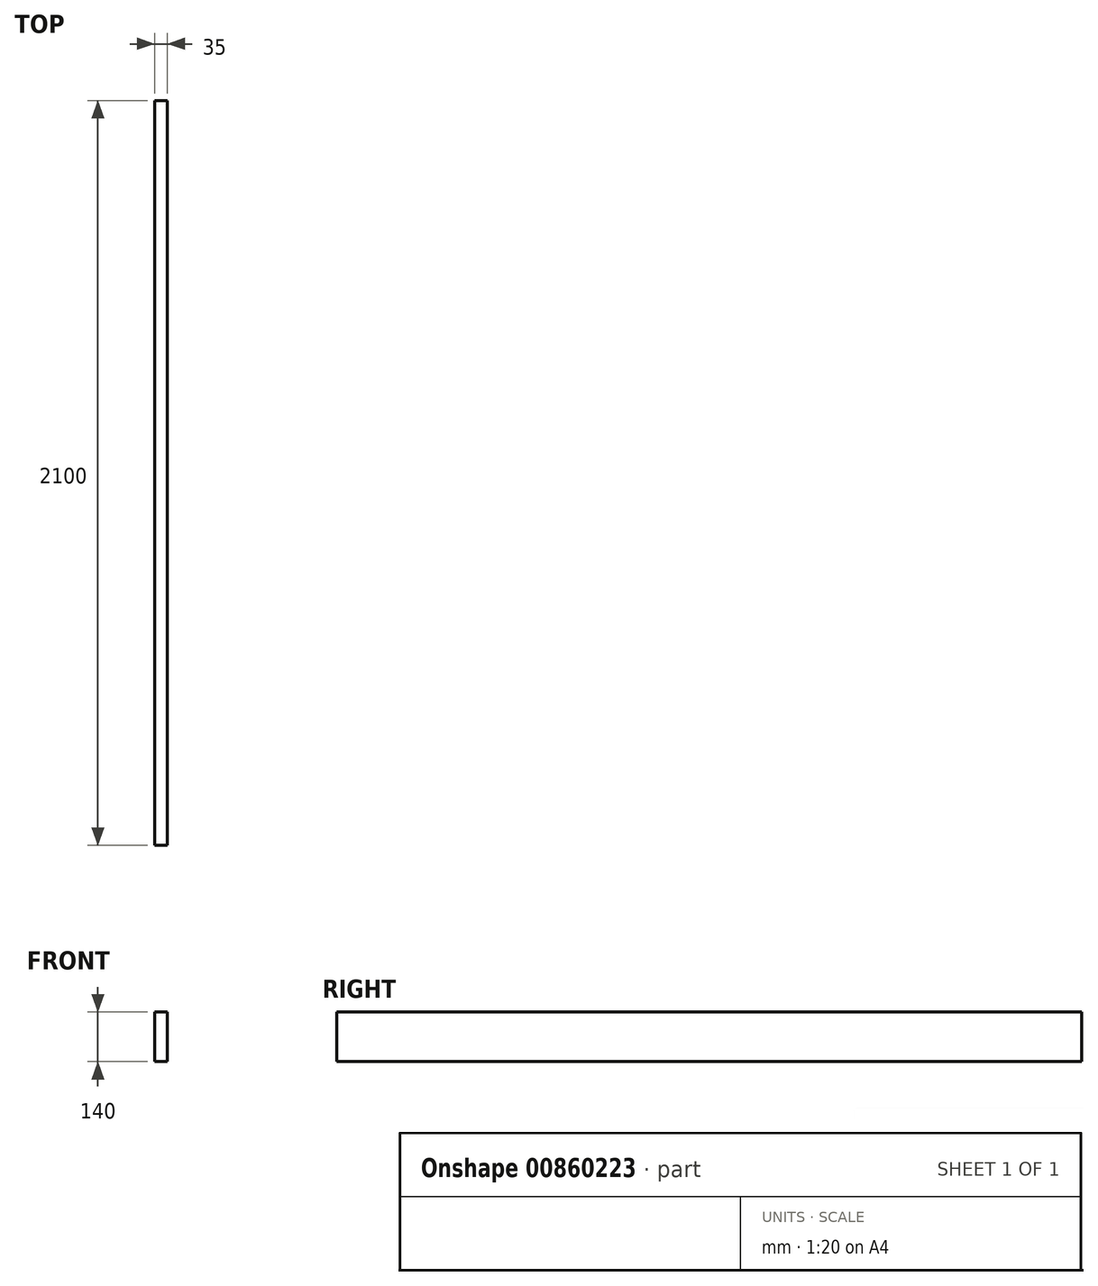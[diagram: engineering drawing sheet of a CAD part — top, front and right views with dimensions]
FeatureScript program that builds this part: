
annotation { "Feature Type Name" : "Feature", "Feature Type Description" : "" }
export const myFeature = defineFeature(function(context is Context, id is Id, definition is map)
    precondition{}
    {
        {
            var Q0;
            Q0=qCreatedBy(makeId("Front.planeOp"),FACE);
            var sketch = newSketch(context, id + "F0", { "sketchPlane" : qUnion([Q0])});
            skLineSegment(sketch, "E0.bottom", {"start": v(0, 0) * mm, "end": v(35, 0) * mm});
            skLineSegment(sketch, "E0.top", {"start": v(0, 140) * mm, "end": v(35, 140) * mm});
            skLineSegment(sketch, "E0.left", {"start": v(0, 0) * mm, "end": v(0, 140) * mm});
            skLineSegment(sketch, "E0.right", {"start": v(35, 0) * mm, "end": v(35, 140) * mm});
            skSolve(sketch);
        }
        {
            var Q0;
            Q0 = qSketchRegion(id + "F0", true);
            extrude(context, id + "F1", {"entities" : qUnion([Q0]), "depth" : 2100 * mm, "offsetDistance" : 25 * mm});
        }
    });
